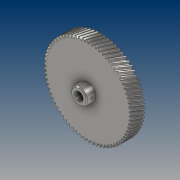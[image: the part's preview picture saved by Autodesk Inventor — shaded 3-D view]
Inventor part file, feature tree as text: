
AUTODESK INVENTOR PART (.ipt)
format: ipt  version: 2021 (Build 250183000, 183)  size: 1,269,248 bytes
history: native  units: mm (DEFAULTED — no unit token found)
features: extrude x4, sketch x4, plane x3, other x3, projected_geometry x2, chamfer x1, pattern_circular x1
ambient origin geometry x8: Origin, YZ Plane, XZ Plane, XY Plane, X Axis, Y Axis, Z Axis, Center Point
bodies: Solid1 (feature_tree)
feature tree (18):
  extrude  "Extrusion1"  Depth=15.0mm TaperAngle=0.0deg
  plane  "Work Plane2"
  plane  "Work Plane8"
  plane  "Work Plane9"
  other  "Spur Gear"
  sketch  "Sketch3"  dims[d16=59.86mm d17=0.0mm d34=0.436332mm]
  extrude  "Extrusion2"  Depth=10.0mm TaperAngle=0.0deg
  extrude  "Extrusion3"  Depth=0.436332mm TaperAngle=0.0deg
  chamfer  "Chamfer1"  [1 undecoded]
  extrude  "Extrusion4"  Depth=15.0mm
  pattern_circular  "Circular Pattern1"  [2 undecoded]
  sketch  "Sketch1"  dims[d0=98.276mm d1=15.0mm d2=0.0mm]
  sketch  "Sketch2"  dims[d3=95.776mm d4=10.0mm d5=0.0mm]
  other  "Srf1"
  projected_geometry  "Projected Loop1"
  sketch  "Sketch4"  dims[d39=0.0mm d41=0.0mm d43=59.86mm d46=59.86mm d47=0.0mm d48=0.0mm d49=10.0mm d50=4.0mm d51=22.0mm d52=0.0mm d53=10.0mm d54=0.0mm d55=1.0mm d56=2.0mm d57=45.0deg d58=2.5mm d59=15.0mm d60=0.0mm d61=20.0mm d62=90.0deg]
  projected_geometry  "Projected Loop2"
  other  "Pitch Diameter"
note: 3 required parameter values undecoded (feature->parameter linkage not recoverable at this tier; creation-order binding heuristic only, values carry confidence <= 0.55)
